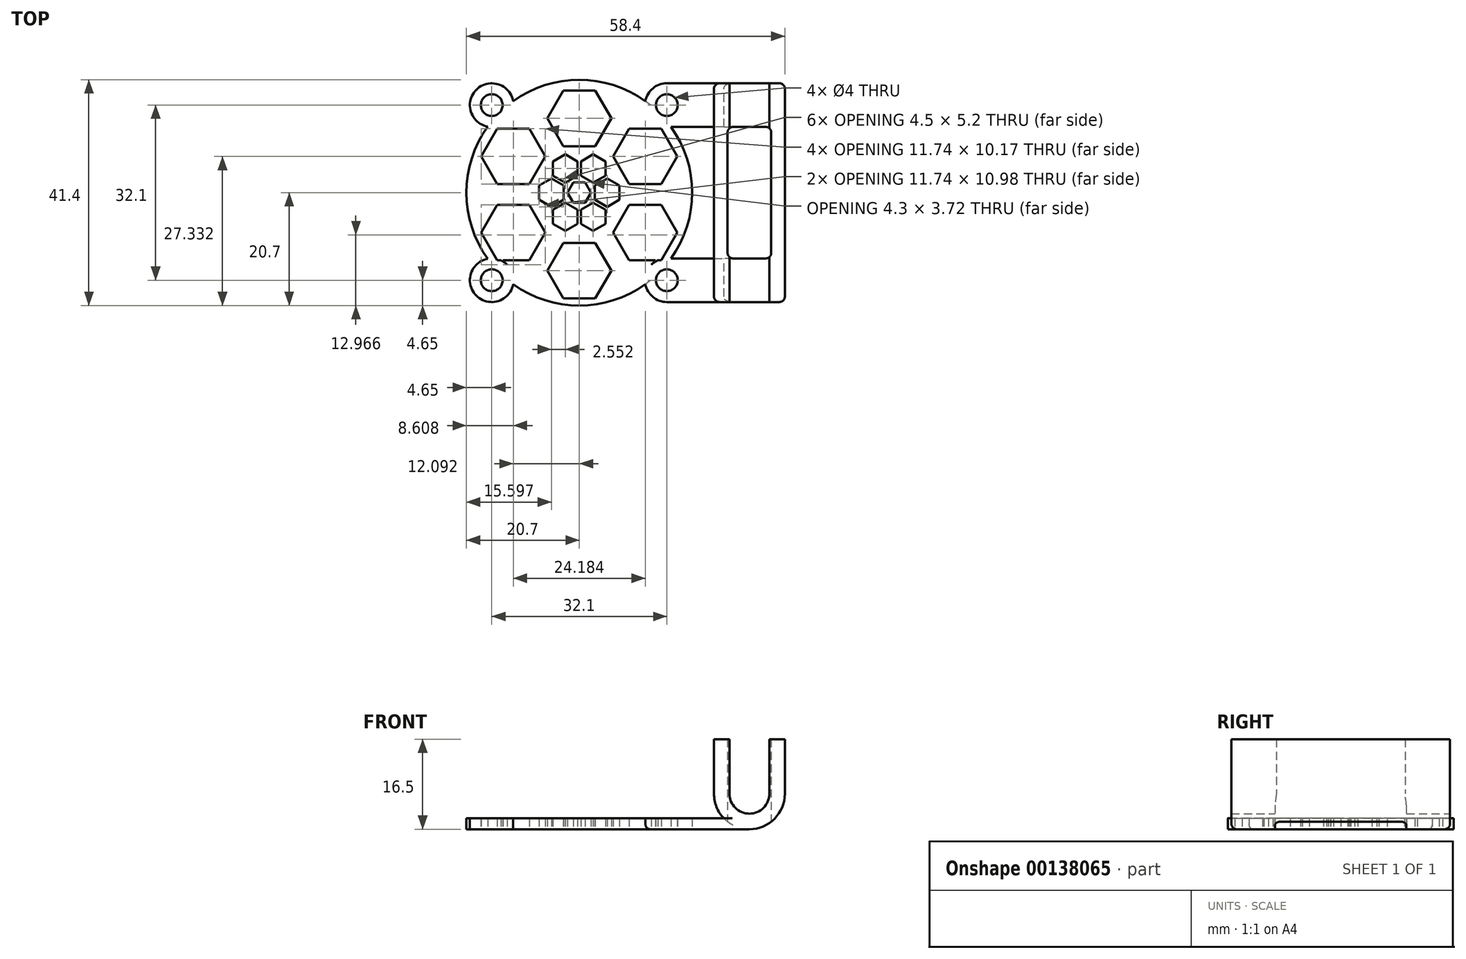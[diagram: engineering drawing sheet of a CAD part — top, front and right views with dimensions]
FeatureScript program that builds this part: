
annotation { "Feature Type Name" : "Feature", "Feature Type Description" : "" }
export const myFeature = defineFeature(function(context is Context, id is Id, definition is map)
    precondition{}
    {
        {
            var Q0;
            Q0=qCreatedBy(makeId("Top.planeOp"),FACE);
            var sketch = newSketch(context, id + "F0", { "sketchPlane" : qUnion([Q0])});
            skCircle(sketch, "E0", {"center": v(-16.05, -16.05) * mm, "radius": 2 * mm});
            skCircle(sketch, "E1", {"center": v(0, 0) * mm, "radius": 20.7 * mm});
            skCircle(sketch, "E2", {"center": v(0, 0) * mm, "radius": 18.7 * mm});
            skCircle(sketch, "E3.cCircle", {"center": v(0, 13.61) * mm, "radius": 5.09 * mm, "construction": true});
            skLineSegment(sketch, "E3.0", {"start": v(-2.94, 18.7) * mm, "end": v(2.94, 18.7) * mm});
            skLineSegment(sketch, "E3.1", {"start": v(2.94, 18.7) * mm, "end": v(5.87, 13.61) * mm});
            skLineSegment(sketch, "E3.2", {"start": v(5.87, 13.61) * mm, "end": v(2.94, 8.53) * mm});
            skLineSegment(sketch, "E3.3", {"start": v(2.94, 8.53) * mm, "end": v(-2.94, 8.53) * mm});
            skLineSegment(sketch, "E3.4", {"start": v(-2.94, 8.53) * mm, "end": v(-5.87, 13.61) * mm});
            skLineSegment(sketch, "E3.5", {"start": v(-5.87, 13.61) * mm, "end": v(-2.94, 18.7) * mm});
            skPoint(sketch, "E3.0.midPoint", {"position": v(0, 18.7) * mm});
            skLineSegment(sketch, "E4.1.0", {"start": v(9.16, 11.72) * mm, "end": v(15.03, 11.72) * mm});
            skLineSegment(sketch, "E4.1.1", {"start": v(15.03, 1.55) * mm, "end": v(9.16, 1.55) * mm});
            skLineSegment(sketch, "E4.1.2", {"start": v(9.16, 1.55) * mm, "end": v(6.22, 6.63) * mm});
            skLineSegment(sketch, "E4.1.3", {"start": v(15.03, 11.72) * mm, "end": v(17.96, 6.63) * mm});
            skLineSegment(sketch, "E4.1.4", {"start": v(6.22, 6.63) * mm, "end": v(9.16, 11.72) * mm});
            skLineSegment(sketch, "E4.1.5", {"start": v(17.96, 6.63) * mm, "end": v(15.03, 1.55) * mm});
            skLineSegment(sketch, "E4.2.0", {"start": v(15.03, -2.25) * mm, "end": v(17.96, -7.33) * mm});
            skLineSegment(sketch, "E4.2.1", {"start": v(9.16, -12.42) * mm, "end": v(6.22, -7.33) * mm});
            skLineSegment(sketch, "E4.2.2", {"start": v(6.22, -7.33) * mm, "end": v(9.16, -2.25) * mm});
            skLineSegment(sketch, "E4.2.3", {"start": v(17.96, -7.33) * mm, "end": v(15.03, -12.42) * mm});
            skLineSegment(sketch, "E4.2.4", {"start": v(9.16, -2.25) * mm, "end": v(15.03, -2.25) * mm});
            skLineSegment(sketch, "E4.2.5", {"start": v(15.03, -12.42) * mm, "end": v(9.16, -12.42) * mm});
            skLineSegment(sketch, "E4.3.0", {"start": v(5.87, -14.31) * mm, "end": v(2.94, -19.4) * mm});
            skLineSegment(sketch, "E4.3.1", {"start": v(-5.87, -14.31) * mm, "end": v(-2.94, -9.23) * mm});
            skLineSegment(sketch, "E4.3.2", {"start": v(-2.94, -9.23) * mm, "end": v(2.94, -9.23) * mm});
            skLineSegment(sketch, "E4.3.3", {"start": v(2.94, -19.4) * mm, "end": v(-2.94, -19.4) * mm});
            skLineSegment(sketch, "E4.3.4", {"start": v(2.94, -9.23) * mm, "end": v(5.87, -14.31) * mm});
            skLineSegment(sketch, "E4.3.5", {"start": v(-2.94, -19.4) * mm, "end": v(-5.87, -14.31) * mm});
            skLineSegment(sketch, "E4.4.0", {"start": v(-9.16, -12.42) * mm, "end": v(-15.03, -12.42) * mm});
            skLineSegment(sketch, "E4.4.1", {"start": v(-15.03, -2.25) * mm, "end": v(-9.16, -2.25) * mm});
            skLineSegment(sketch, "E4.4.2", {"start": v(-9.16, -2.25) * mm, "end": v(-6.22, -7.33) * mm});
            skLineSegment(sketch, "E4.4.3", {"start": v(-15.03, -12.42) * mm, "end": v(-17.96, -7.33) * mm});
            skLineSegment(sketch, "E4.4.4", {"start": v(-6.22, -7.33) * mm, "end": v(-9.16, -12.42) * mm});
            skLineSegment(sketch, "E4.4.5", {"start": v(-17.96, -7.33) * mm, "end": v(-15.03, -2.25) * mm});
            skLineSegment(sketch, "E4.5.0", {"start": v(-15.03, 1.55) * mm, "end": v(-17.96, 6.63) * mm});
            skLineSegment(sketch, "E4.5.1", {"start": v(-9.16, 11.72) * mm, "end": v(-6.22, 6.63) * mm});
            skLineSegment(sketch, "E4.5.2", {"start": v(-6.22, 6.63) * mm, "end": v(-9.16, 1.55) * mm});
            skLineSegment(sketch, "E4.5.3", {"start": v(-17.96, 6.63) * mm, "end": v(-15.03, 11.72) * mm});
            skLineSegment(sketch, "E4.5.4", {"start": v(-9.16, 1.55) * mm, "end": v(-15.03, 1.55) * mm});
            skLineSegment(sketch, "E4.5.5", {"start": v(-15.03, 11.72) * mm, "end": v(-9.16, 11.72) * mm});
            skLineSegment(sketch, "E4.anchor1", {"start": v(0, -0.35) * mm, "end": v(-2.94, 18.7) * mm, "construction": true});
            skLineSegment(sketch, "E4.anchor2", {"start": v(0, -0.35) * mm, "end": v(-17.96, 6.63) * mm, "construction": true});
            skLineSegment(sketch, "E5", {"start": v(2.94, 8.53) * mm, "end": v(6.22, 6.63) * mm, "construction": true});
            skLineSegment(sketch, "E6", {"start": v(-16.05, -16.05) * mm, "end": v(0, 0) * mm, "construction": true});
            skCircle(sketch, "E7", {"center": v(-16.05, -16.05) * mm, "radius": 4 * mm});
            skCircle(sketch, "E8.0.1.0", {"center": v(-16.05, 16.05) * mm, "radius": 4 * mm});
            skCircle(sketch, "E8.0.1.1", {"center": v(-16.05, 16.05) * mm, "radius": 2 * mm});
            skCircle(sketch, "E8.1.0.0", {"center": v(16.05, -16.05) * mm, "radius": 4 * mm});
            skCircle(sketch, "E8.1.0.1", {"center": v(16.05, -16.05) * mm, "radius": 2 * mm});
            skCircle(sketch, "E8.1.1.0", {"center": v(16.05, 16.05) * mm, "radius": 4 * mm});
            skCircle(sketch, "E8.1.1.1", {"center": v(16.05, 16.05) * mm, "radius": 2 * mm});
            skLineSegment(sketch, "E8.direction1", {"start": v(-16.05, -16.05) * mm, "end": v(16.05, -16.05) * mm, "construction": true});
            skLineSegment(sketch, "E8.direction2", {"start": v(-16.05, -16.05) * mm, "end": v(-16.05, 16.05) * mm, "construction": true});
            skCircle(sketch, "E9.cCircle", {"center": v(2.55, 4.42) * mm, "radius": 2.25 * mm, "construction": true});
            skLineSegment(sketch, "E9.0", {"start": v(2.55, 7.02) * mm, "end": v(4.8, 5.72) * mm});
            skLineSegment(sketch, "E9.1", {"start": v(4.8, 5.72) * mm, "end": v(4.8, 3.12) * mm});
            skLineSegment(sketch, "E9.2", {"start": v(4.8, 3.12) * mm, "end": v(2.55, 1.82) * mm});
            skLineSegment(sketch, "E9.3", {"start": v(2.55, 1.82) * mm, "end": v(0.3, 3.12) * mm});
            skLineSegment(sketch, "E9.4", {"start": v(0.3, 3.12) * mm, "end": v(0.3, 5.72) * mm});
            skLineSegment(sketch, "E9.5", {"start": v(0.3, 5.72) * mm, "end": v(2.55, 7.02) * mm});
            skPoint(sketch, "E9.0.midPoint", {"position": v(3.68, 6.37) * mm});
            skLineSegment(sketch, "E10", {"start": v(3.68, 6.37) * mm, "end": v(4.43, 7.67) * mm, "construction": true});
            skCircle(sketch, "E11.cCircle", {"center": v(0, 0) * mm, "radius": 1.86 * mm, "construction": true});
            skLineSegment(sketch, "E11.0", {"start": v(-1.08, 1.86) * mm, "end": v(1.08, 1.86) * mm});
            skLineSegment(sketch, "E11.1", {"start": v(1.08, 1.86) * mm, "end": v(2.15, 0) * mm});
            skLineSegment(sketch, "E11.2", {"start": v(2.15, 0) * mm, "end": v(1.08, -1.86) * mm});
            skLineSegment(sketch, "E11.3", {"start": v(1.08, -1.86) * mm, "end": v(-1.08, -1.86) * mm});
            skLineSegment(sketch, "E11.4", {"start": v(-1.08, -1.86) * mm, "end": v(-2.15, 0) * mm});
            skLineSegment(sketch, "E11.5", {"start": v(-2.15, 0) * mm, "end": v(-1.08, 1.86) * mm});
            skPoint(sketch, "E11.0.midPoint", {"position": v(0, 1.86) * mm});
            skLineSegment(sketch, "E12", {"start": v(1.08, 1.86) * mm, "end": v(1.43, 2.47) * mm, "construction": true});
            skLineSegment(sketch, "E13.1.0", {"start": v(-4.8, 3.12) * mm, "end": v(-4.8, 5.72) * mm});
            skLineSegment(sketch, "E13.1.1", {"start": v(-4.8, 5.72) * mm, "end": v(-2.55, 7.02) * mm});
            skLineSegment(sketch, "E13.1.2", {"start": v(-2.55, 7.02) * mm, "end": v(-0.3, 5.72) * mm});
            skLineSegment(sketch, "E13.1.3", {"start": v(-0.3, 5.72) * mm, "end": v(-0.3, 3.12) * mm});
            skLineSegment(sketch, "E13.1.4", {"start": v(-0.3, 3.12) * mm, "end": v(-2.55, 1.82) * mm});
            skLineSegment(sketch, "E13.1.5", {"start": v(-2.55, 1.82) * mm, "end": v(-4.8, 3.12) * mm});
            skLineSegment(sketch, "E13.2.0", {"start": v(-5.1, -2.6) * mm, "end": v(-7.35, -1.3) * mm});
            skLineSegment(sketch, "E13.2.1", {"start": v(-7.35, -1.3) * mm, "end": v(-7.35, 1.3) * mm});
            skLineSegment(sketch, "E13.2.2", {"start": v(-7.35, 1.3) * mm, "end": v(-5.1, 2.6) * mm});
            skLineSegment(sketch, "E13.2.3", {"start": v(-5.1, 2.6) * mm, "end": v(-2.85, 1.3) * mm});
            skLineSegment(sketch, "E13.2.4", {"start": v(-2.85, 1.3) * mm, "end": v(-2.85, -1.3) * mm});
            skLineSegment(sketch, "E13.2.5", {"start": v(-2.85, -1.3) * mm, "end": v(-5.1, -2.6) * mm});
            skLineSegment(sketch, "E13.3.0", {"start": v(-0.3, -5.72) * mm, "end": v(-2.55, -7.02) * mm});
            skLineSegment(sketch, "E13.3.1", {"start": v(-2.55, -7.02) * mm, "end": v(-4.8, -5.72) * mm});
            skLineSegment(sketch, "E13.3.2", {"start": v(-4.8, -5.72) * mm, "end": v(-4.8, -3.12) * mm});
            skLineSegment(sketch, "E13.3.3", {"start": v(-4.8, -3.12) * mm, "end": v(-2.55, -1.82) * mm});
            skLineSegment(sketch, "E13.3.4", {"start": v(-2.55, -1.82) * mm, "end": v(-0.3, -3.12) * mm});
            skLineSegment(sketch, "E13.3.5", {"start": v(-0.3, -3.12) * mm, "end": v(-0.3, -5.72) * mm});
            skLineSegment(sketch, "E13.4.0", {"start": v(4.8, -3.12) * mm, "end": v(4.8, -5.72) * mm});
            skLineSegment(sketch, "E13.4.1", {"start": v(4.8, -5.72) * mm, "end": v(2.55, -7.02) * mm});
            skLineSegment(sketch, "E13.4.2", {"start": v(2.55, -7.02) * mm, "end": v(0.3, -5.72) * mm});
            skLineSegment(sketch, "E13.4.3", {"start": v(0.3, -5.72) * mm, "end": v(0.3, -3.12) * mm});
            skLineSegment(sketch, "E13.4.4", {"start": v(0.3, -3.12) * mm, "end": v(2.55, -1.82) * mm});
            skLineSegment(sketch, "E13.4.5", {"start": v(2.55, -1.82) * mm, "end": v(4.8, -3.12) * mm});
            skLineSegment(sketch, "E13.5.0", {"start": v(5.1, 2.6) * mm, "end": v(7.35, 1.3) * mm});
            skLineSegment(sketch, "E13.5.1", {"start": v(7.35, 1.3) * mm, "end": v(7.35, -1.3) * mm});
            skLineSegment(sketch, "E13.5.2", {"start": v(7.35, -1.3) * mm, "end": v(5.1, -2.6) * mm});
            skLineSegment(sketch, "E13.5.3", {"start": v(5.1, -2.6) * mm, "end": v(2.85, -1.3) * mm});
            skLineSegment(sketch, "E13.5.4", {"start": v(2.85, -1.3) * mm, "end": v(2.85, 1.3) * mm});
            skLineSegment(sketch, "E13.5.5", {"start": v(2.85, 1.3) * mm, "end": v(5.1, 2.6) * mm});
            skLineSegment(sketch, "E14", {"start": v(16.05, 16.05) * mm, "end": v(16.05, 20.05) * mm, "construction": true});
            skLineSegment(sketch, "E15", {"start": v(16.05, -16.05) * mm, "end": v(16.05, -20.05) * mm, "construction": true});
            skLineSegment(sketch, "E16", {"start": v(16.05, -16.05) * mm, "end": v(16.05, -12.05) * mm, "construction": true});
            skLineSegment(sketch, "E17", {"start": v(16.05, 16.05) * mm, "end": v(16.05, 12.05) * mm, "construction": true});
            skLineSegment(sketch, "E18", {"start": v(0, -0.35) * mm, "end": v(20.7, -0.35) * mm, "construction": true});
            skLineSegment(sketch, "E19", {"start": v(16.05, 20.05) * mm, "end": v(37.7, 20.05) * mm});
            skLineSegment(sketch, "E20", {"start": v(37.7, 20.05) * mm, "end": v(37.7, -20.05) * mm});
            skLineSegment(sketch, "E21", {"start": v(37.7, -20.05) * mm, "end": v(16.05, -20.05) * mm});
            skLineSegment(sketch, "E22", {"start": v(16.05, -12.05) * mm, "end": v(24.7, -12.05) * mm});
            skLineSegment(sketch, "E23", {"start": v(24.7, -12.05) * mm, "end": v(24.7, 12.05) * mm});
            skLineSegment(sketch, "E24", {"start": v(24.7, 12.05) * mm, "end": v(16.05, 12.05) * mm});
            skLineSegment(sketch, "E25.bottom", {"start": v(27.2, 20.05) * mm, "end": v(35.2, 20.05) * mm});
            skLineSegment(sketch, "E25.top", {"start": v(27.2, -20.05) * mm, "end": v(35.2, -20.05) * mm});
            skLineSegment(sketch, "E25.left", {"start": v(27.2, 20.05) * mm, "end": v(27.2, -20.05) * mm});
            skLineSegment(sketch, "E25.right", {"start": v(35.2, 20.05) * mm, "end": v(35.2, -20.05) * mm});
            skLineSegment(sketch, "E26", {"start": v(24.7, 12.05) * mm, "end": v(24.7, 20.05) * mm});
            skLineSegment(sketch, "E27", {"start": v(24.7, -12.05) * mm, "end": v(24.7, -20.05) * mm});
            skLineSegment(sketch, "E28.bottom", {"start": v(24.7, 12.05) * mm, "end": v(37.7, 12.05) * mm});
            skLineSegment(sketch, "E28.top", {"start": v(24.7, -12.05) * mm, "end": v(37.7, -12.05) * mm});
            skLineSegment(sketch, "E28.left", {"start": v(24.7, 12.05) * mm, "end": v(24.7, -12.05) * mm});
            skLineSegment(sketch, "E28.right", {"start": v(37.7, 12.05) * mm, "end": v(37.7, -12.05) * mm});
            skSolve(sketch);
        }
        {
            var Q0;
            {var subQ0=sQuery(id+"F0.wireOp",EDGE,"E8.0.1.0");var subQ1=sQuery(id+"F0.wireOp",EDGE,"E1");var subQ2=makeQuery(id+"F0.imprint","INTERSECT",VERTEX,{"disambiguationData":[OD(0.0)],"derivedFrom":[subQ1,subQ0]});Q0=makeQuery(id+"F0.imprint","IMPRINT",FACE,{"disambiguationData":[TD([[makeQuery(id+"F0.imprint","IMPRINT",EDGE,{"disambiguationData":[TD([[subQ2,-1.0]])],"derivedFrom":subQ1}),1.0]])]});}
            var Q1;
            {var subQ8=sQuery(id+"F0.wireOp",EDGE,"E8.1.1.0");var subQ12=sQuery(id+"F0.wireOp",EDGE,"E1");var subQ13=makeQuery(id+"F0.imprint","INTERSECT",VERTEX,{"disambiguationData":[OD(1.0)],"derivedFrom":[subQ12,subQ8]});Q1=makeQuery(id+"F0.imprint","IMPRINT",FACE,{"disambiguationData":[TD([[makeQuery(id+"F0.imprint","IMPRINT",EDGE,{"disambiguationData":[TD([[subQ13,-1.0]])],"derivedFrom":subQ12}),1.0]])]});}
            var Q2;
            {var subQ0=sQuery(id+"F0.wireOp",EDGE,"E1");var subQ1=makeQuery(id+"F0.imprint","INTERSECT",VERTEX,{"derivedFrom":[subQ0,sQuery(id+"F0.wireOp",EDGE,"E8.1.1.1")]});Q2=makeQuery(id+"F0.imprint","IMPRINT",FACE,{"disambiguationData":[TD([[makeQuery(id+"F0.imprint","IMPRINT",EDGE,{"disambiguationData":[TD([[subQ1,1.0]])],"derivedFrom":subQ0}),1.0]])]});}
            var Q3;
            {var subQ8=sQuery(id+"F0.wireOp",EDGE,"E8.1.1.0");var subQ9=sQuery(id+"F0.wireOp",EDGE,"E1");var subQ10=makeQuery(id+"F0.imprint","INTERSECT",VERTEX,{"disambiguationData":[OD(0.0)],"derivedFrom":[subQ9,subQ8]});Q3=makeQuery(id+"F0.imprint","IMPRINT",FACE,{"disambiguationData":[TD([[makeQuery(id+"F0.imprint","IMPRINT",EDGE,{"disambiguationData":[TD([[subQ10,1.0]])],"derivedFrom":subQ9}),1.0]])]});}
            var Q4;
            {var subQ0=sQuery(id+"F0.wireOp",EDGE,"E8.1.0.0");var subQ1=sQuery(id+"F0.wireOp",EDGE,"E1");var subQ2=makeQuery(id+"F0.imprint","INTERSECT",VERTEX,{"disambiguationData":[OD(0.0)],"derivedFrom":[subQ1,subQ0]});Q4=makeQuery(id+"F0.imprint","IMPRINT",FACE,{"disambiguationData":[TD([[makeQuery(id+"F0.imprint","IMPRINT",EDGE,{"disambiguationData":[TD([[subQ2,-1.0]])],"derivedFrom":subQ1}),1.0]])]});}
            var Q5;
            {var subQ11=sQuery(id+"F0.wireOp",EDGE,"E7");var subQ13=sQuery(id+"F0.wireOp",EDGE,"E1");var subQ14=makeQuery(id+"F0.imprint","INTERSECT",VERTEX,{"disambiguationData":[OD(1.0)],"derivedFrom":[subQ13,subQ11]});Q5=makeQuery(id+"F0.imprint","IMPRINT",FACE,{"disambiguationData":[TD([[makeQuery(id+"F0.imprint","IMPRINT",EDGE,{"disambiguationData":[TD([[subQ14,-1.0]])],"derivedFrom":subQ13}),1.0]])]});}
            var Q6;
            {var subQ0=sQuery(id+"F0.wireOp",EDGE,"E1");var subQ1=makeQuery(id+"F0.imprint","INTERSECT",VERTEX,{"derivedFrom":[sQuery(id+"F0.wireOp",EDGE,"E0"),subQ0]});Q6=makeQuery(id+"F0.imprint","IMPRINT",FACE,{"disambiguationData":[TD([[makeQuery(id+"F0.imprint","IMPRINT",EDGE,{"disambiguationData":[TD([[subQ1,1.0]])],"derivedFrom":subQ0}),1.0]])]});}
            var Q7;
            {var subQ8=sQuery(id+"F0.wireOp",EDGE,"E8.0.1.0");var subQ14=sQuery(id+"F0.wireOp",EDGE,"E1");var subQ15=makeQuery(id+"F0.imprint","INTERSECT",VERTEX,{"disambiguationData":[OD(1.0)],"derivedFrom":[subQ14,subQ8]});Q7=makeQuery(id+"F0.imprint","IMPRINT",FACE,{"disambiguationData":[TD([[makeQuery(id+"F0.imprint","IMPRINT",EDGE,{"disambiguationData":[TD([[subQ15,-1.0]])],"derivedFrom":subQ14}),1.0]])]});}
            var Q8;
            {var subQ3=sQuery(id+"F0.wireOp",EDGE,"E8.0.1.1");Q8=makeQuery(id+"F0.imprint","IMPRINT",FACE,{"disambiguationData":[TD([[makeQuery(id+"F0.imprint","IMPRINT",EDGE,{"derivedFrom":subQ3}),-1.0]])]});}
            var Q9;
            {var subQ0=sQuery(id+"F0.wireOp",EDGE,"E8.1.1.1");Q9=makeQuery(id+"F0.imprint","IMPRINT",FACE,{"disambiguationData":[TD([[makeQuery(id+"F0.imprint","IMPRINT",EDGE,{"derivedFrom":subQ0}),-1.0]])]});}
            var Q10;
            {var subQ3=sQuery(id+"F0.wireOp",EDGE,"E8.1.0.1");Q10=makeQuery(id+"F0.imprint","IMPRINT",FACE,{"disambiguationData":[TD([[makeQuery(id+"F0.imprint","IMPRINT",EDGE,{"derivedFrom":subQ3}),-1.0]])]});}
            var Q11;
            {var subQ0=sQuery(id+"F0.wireOp",EDGE,"E0");Q11=makeQuery(id+"F0.imprint","IMPRINT",FACE,{"disambiguationData":[TD([[makeQuery(id+"F0.imprint","IMPRINT",EDGE,{"derivedFrom":subQ0}),-1.0]])]});}
            var Q12;
            {var subQ39=sQuery(id+"F0.wireOp",EDGE,"E3.2");Q12=makeQuery(id+"F0.imprint","IMPRINT",FACE,{"disambiguationData":[TD([[makeQuery(id+"F0.imprint","IMPRINT",EDGE,{"derivedFrom":subQ39}),1.0]])]});}
            var Q13;
            {var subQ5=sQuery(id+"F0.wireOp",EDGE,"E8.1.1.0");var subQ6=sQuery(id+"F0.wireOp",EDGE,"E1");var subQ7=makeQuery(id+"F0.imprint","INTERSECT",VERTEX,{"disambiguationData":[OD(0.0)],"derivedFrom":[subQ6,subQ5]});Q13=makeQuery(id+"F0.imprint","IMPRINT",FACE,{"disambiguationData":[TD([[makeQuery(id+"F0.imprint","IMPRINT",EDGE,{"disambiguationData":[TD([[subQ7,-1.0]])],"derivedFrom":subQ6}),1.0]])]});}
            var Q14;
            {var subQ11=sQuery(id+"F0.wireOp",EDGE,"E24");var subQ14=sQuery(id+"F0.wireOp",EDGE,"E1");var subQ15=makeQuery(id+"F0.imprint","INTERSECT",VERTEX,{"derivedFrom":[subQ14,subQ11]});Q14=makeQuery(id+"F0.imprint","IMPRINT",FACE,{"disambiguationData":[TD([[makeQuery(id+"F0.imprint","IMPRINT",EDGE,{"disambiguationData":[TD([[subQ15,1.0]])],"derivedFrom":subQ14}),1.0]])]});}
            var Q15;
            {var subQ0=sQuery(id+"F0.wireOp",EDGE,"E26");Q15=makeQuery(id+"F0.imprint","IMPRINT",FACE,{"disambiguationData":[TD([[makeQuery(id+"F0.imprint","IMPRINT",EDGE,{"derivedFrom":subQ0}),1.0]])]});}
            var Q16;
            {var subQ0=sQuery(id+"F0.wireOp",EDGE,"E27");Q16=makeQuery(id+"F0.imprint","IMPRINT",FACE,{"disambiguationData":[TD([[makeQuery(id+"F0.imprint","IMPRINT",EDGE,{"derivedFrom":subQ0}),-1.0]])]});}
            var Q17;
            {var subQ0=sQuery(id+"F0.wireOp",EDGE,"E8.1.1.0");var subQ1=sQuery(id+"F0.wireOp",EDGE,"E1");var subQ2=makeQuery(id+"F0.imprint","INTERSECT",VERTEX,{"disambiguationData":[OD(1.0)],"derivedFrom":[subQ1,subQ0]});Q17=makeQuery(id+"F0.imprint","IMPRINT",FACE,{"disambiguationData":[TD([[makeQuery(id+"F0.imprint","IMPRINT",EDGE,{"disambiguationData":[TD([[subQ2,1.0]])],"derivedFrom":subQ1}),1.0]])]});}
            var Q18;
            {var subQ0=sQuery(id+"F0.wireOp",EDGE,"E8.1.0.0");var subQ1=sQuery(id+"F0.wireOp",EDGE,"E1");var subQ2=makeQuery(id+"F0.imprint","INTERSECT",VERTEX,{"disambiguationData":[OD(1.0)],"derivedFrom":[subQ1,subQ0]});Q18=makeQuery(id+"F0.imprint","IMPRINT",FACE,{"disambiguationData":[TD([[makeQuery(id+"F0.imprint","IMPRINT",EDGE,{"disambiguationData":[TD([[subQ2,-1.0]])],"derivedFrom":subQ1}),1.0]])]});}
            extrude(context, id + "F1", {"entities" : qUnion([Q0, Q1, Q2, Q3, Q4, Q5, Q6, Q7, Q8, Q9, Q10, Q11, Q12, Q13, Q14, Q15, Q16, Q17, Q18]), "depth" : 2 * mm});
        }
        {
            var Q0;
            Q0=makeQuery(id+"F1.opExtrude","SWEPT_FACE",FACE,{"disambiguationData":[OSD([sQuery(id+"F0.wireOp",EDGE,"E19")])]});
            var sketch = newSketch(context, id + "F2", { "sketchPlane" : qUnion([Q0])});
            skLineSegment(sketch, "E29.top", {"start": v(-24.7, 0) * mm, "end": v(-37.7, 0) * mm, "construction": true});
            skLineSegment(sketch, "E29.left", {"start": v(-24.7, 2) * mm, "end": v(-24.7, 0) * mm, "construction": true});
            skLineSegment(sketch, "E29.right", {"start": v(-37.7, 2) * mm, "end": v(-37.7, 0) * mm, "construction": true});
            skArc(sketch, "E30", {"start": v(-37.7, 6.5) * mm, "mid": v(-31.2, 0) * mm, "end": v(-24.7, 6.5) * mm});
            skArc(sketch, "E31", {"start": v(-27.55, 6.5) * mm, "mid": v(-31.2, 2.85) * mm, "end": v(-34.85, 6.5) * mm});
            skLineSegment(sketch, "E32", {"start": v(-37.7, 6.5) * mm, "end": v(-34.85, 6.5) * mm});
            skLineSegment(sketch, "E33", {"start": v(-27.55, 6.5) * mm, "end": v(-24.7, 6.5) * mm});
            skPoint(sketch, "E34", {"position": v(-26.5, 2) * mm});
            skPoint(sketch, "E35", {"position": v(-31.2, 0) * mm});
            skSolve(sketch);
        }
        {
            var Q0;
            Q0=makeQuery(id+"F1.opExtrude","SWEPT_FACE",FACE,{"disambiguationData":[OSD([sQuery(id+"F0.wireOp",EDGE,"E26")])]});
            var Q1;
            Q1=makeQuery(id+"F1.opExtrude","SWEPT_FACE",FACE,{"disambiguationData":[OSD([sQuery(id+"F0.wireOp",EDGE,"E27")])]});
            extrude(context, id + "F3", {"entities" : qUnion([Q0, Q1]), "operationType" : NewBodyOperationType.ADD, "depth" : 6.5 * mm});
        }
        {
            var Q0;
            Q0=makeQuery(id+"F2.imprint","IMPRINT",FACE,{"disambiguationData":[TD([[makeQuery(id+"F2.imprint","IMPRINT",EDGE,{"derivedFrom":sQuery(id+"F2.wireOp",EDGE,"E30")}),1.0]])]});
            var Q1;
            {var subQ0=sQuery(id+"F0.wireOp",EDGE,"E21");Q1=makeQuery(id+"F3.boolean.opBoolean","MERGE",FACE,{"derivedFrom":[makeQuery(id+"F1.opExtrude","SWEPT_FACE",FACE,{"disambiguationData":[OSD([subQ0])]}),makeQuery(id+"F3.opExtrude","SWEPT_FACE",FACE,{"disambiguationData":[OSD([subQ0,sQuery(id+"F0.wireOp",EDGE,"E27")])]})]});}
            extrude(context, id + "F4", {"entities" : qUnion([Q0]), "operationType" : NewBodyOperationType.ADD, "endBound" : BoundingType.UP_TO_SURFACE, "oppositeDirection" : true, "endBoundEntityFace" : qUnion([Q1]), "depth" : 25 * mm});
        }
        {
            var Q0;
            Q0=makeQuery(id+"F4.opExtrude","SWEPT_FACE",FACE,{"disambiguationData":[OSD([sQuery(id+"F2.wireOp",EDGE,"E33")])]});
            var Q1;
            Q1=makeQuery(id+"F4.opExtrude","SWEPT_FACE",FACE,{"disambiguationData":[OSD([sQuery(id+"F2.wireOp",EDGE,"E32")])]});
            extrude(context, id + "F5", {"entities" : qUnion([Q0, Q1]), "operationType" : NewBodyOperationType.ADD, "depth" : 10 * mm});
        }
        {
            var Q0;
            {var subQ0=sQuery(id+"F0.wireOp",EDGE,"E28.bottom");var subQ1=sQuery(id+"F0.wireOp",EDGE,"E25.left");var subQ2=makeQuery(id+"F0.imprint","INTERSECT",VERTEX,{"derivedFrom":[subQ1,subQ0]});Q0=makeQuery(id+"F0.imprint","IMPRINT",FACE,{"disambiguationData":[TD([[makeQuery(id+"F0.imprint","IMPRINT",EDGE,{"disambiguationData":[TD([[subQ2,-1.0]])],"derivedFrom":subQ1}),1.0]])]});}
            var Q1;
            {var subQ5=sQuery(id+"F0.wireOp",EDGE,"E28.left");Q1=makeQuery(id+"F0.imprint","IMPRINT",FACE,{"disambiguationData":[TD([[makeQuery(id+"F0.imprint","IMPRINT",EDGE,{"derivedFrom":subQ5}),1.0]])]});}
            var Q2;
            {var subQ5=sQuery(id+"F0.wireOp",EDGE,"E28.right");Q2=makeQuery(id+"F0.imprint","IMPRINT",FACE,{"disambiguationData":[TD([[makeQuery(id+"F0.imprint","IMPRINT",EDGE,{"derivedFrom":subQ5}),-1.0]])]});}
            var Q3;
            Q3=makeQuery(id+"F5.opExtrude","CAP_FACE",FACE,{"disambiguationData":[OSD([sQuery(id+"F2.wireOp",EDGE,"E32")])],"isStart":false});
            extrude(context, id + "F6", {"entities" : qUnion([Q0, Q1, Q2]), "operationType" : NewBodyOperationType.REMOVE, "endBound" : BoundingType.UP_TO_SURFACE, "endBoundEntityFace" : qUnion([Q3]), "depth" : 25 * mm});
        }
        {
            var Q0;
            Q0=makeQuery(id+"F5.opExtrude","SWEPT_EDGE",EDGE,{"disambiguationData":[OSD([sQuery(id+"F0.wireOp",EDGE,"E21"),sQuery(id+"F0.wireOp",EDGE,"E27"),sQuery(id+"F2.wireOp",EDGE,"E30"),sQuery(id+"F2.wireOp",EDGE,"E33")])]});
            var Q1;
            Q1=makeQuery(id+"F5.opExtrude","SWEPT_EDGE",EDGE,{"disambiguationData":[OSD([sQuery(id+"F0.wireOp",EDGE,"E21"),sQuery(id+"F0.wireOp",EDGE,"E27"),sQuery(id+"F2.wireOp",EDGE,"E30"),sQuery(id+"F2.wireOp",EDGE,"E32")])]});
            var Q2;
            Q2=makeQuery(id+"F5.opExtrude","SWEPT_EDGE",EDGE,{"disambiguationData":[OSD([sQuery(id+"F2.wireOp",EDGE,"E30"),sQuery(id+"F2.wireOp",EDGE,"E33")])]});
            var Q3;
            Q3=makeQuery(id+"F5.opExtrude","SWEPT_EDGE",EDGE,{"disambiguationData":[OSD([sQuery(id+"F2.wireOp",EDGE,"E30"),sQuery(id+"F2.wireOp",EDGE,"E32")])]});
            var Q4;
            Q4=makeQuery(id+"F6.boolean.opBoolean","COPY",EDGE,{"derivedFrom":makeQuery(id+"F6.opExtrude","SWEPT_EDGE",EDGE,{"disambiguationData":[OSD([sQuery(id+"F0.wireOp",EDGE,"E24"),sQuery(id+"F0.wireOp",EDGE,"E26"),sQuery(id+"F0.wireOp",EDGE,"E28.bottom"),sQuery(id+"F0.wireOp",EDGE,"E28.left")])]})});
            var Q5;
            Q5=makeQuery(id+"F6.boolean.opBoolean","COPY",EDGE,{"derivedFrom":makeQuery(id+"F6.opExtrude","SWEPT_EDGE",EDGE,{"disambiguationData":[OSD([sQuery(id+"F0.wireOp",EDGE,"E20"),sQuery(id+"F0.wireOp",EDGE,"E28.bottom"),sQuery(id+"F0.wireOp",EDGE,"E28.right")])]})});
            var Q6;
            Q6=makeQuery(id+"F6.boolean.opBoolean","COPY",EDGE,{"derivedFrom":makeQuery(id+"F6.opExtrude","SWEPT_EDGE",EDGE,{"disambiguationData":[OSD([sQuery(id+"F0.wireOp",EDGE,"E22"),sQuery(id+"F0.wireOp",EDGE,"E27"),sQuery(id+"F0.wireOp",EDGE,"E28.top"),sQuery(id+"F0.wireOp",EDGE,"E28.left")])]})});
            var Q7;
            Q7=makeQuery(id+"F6.boolean.opBoolean","COPY",EDGE,{"derivedFrom":makeQuery(id+"F6.opExtrude","SWEPT_EDGE",EDGE,{"disambiguationData":[OSD([sQuery(id+"F0.wireOp",EDGE,"E20"),sQuery(id+"F0.wireOp",EDGE,"E28.top"),sQuery(id+"F0.wireOp",EDGE,"E28.right")])]})});
            fillet(context, id + "F7", {"entities" : qUnion([Q0, Q1, Q2, Q3, Q4, Q5, Q6, Q7]), "radius" : 1 * mm, "tangentPropagation" : true, "allowEdgeOverflow" : false});
        }
    });
